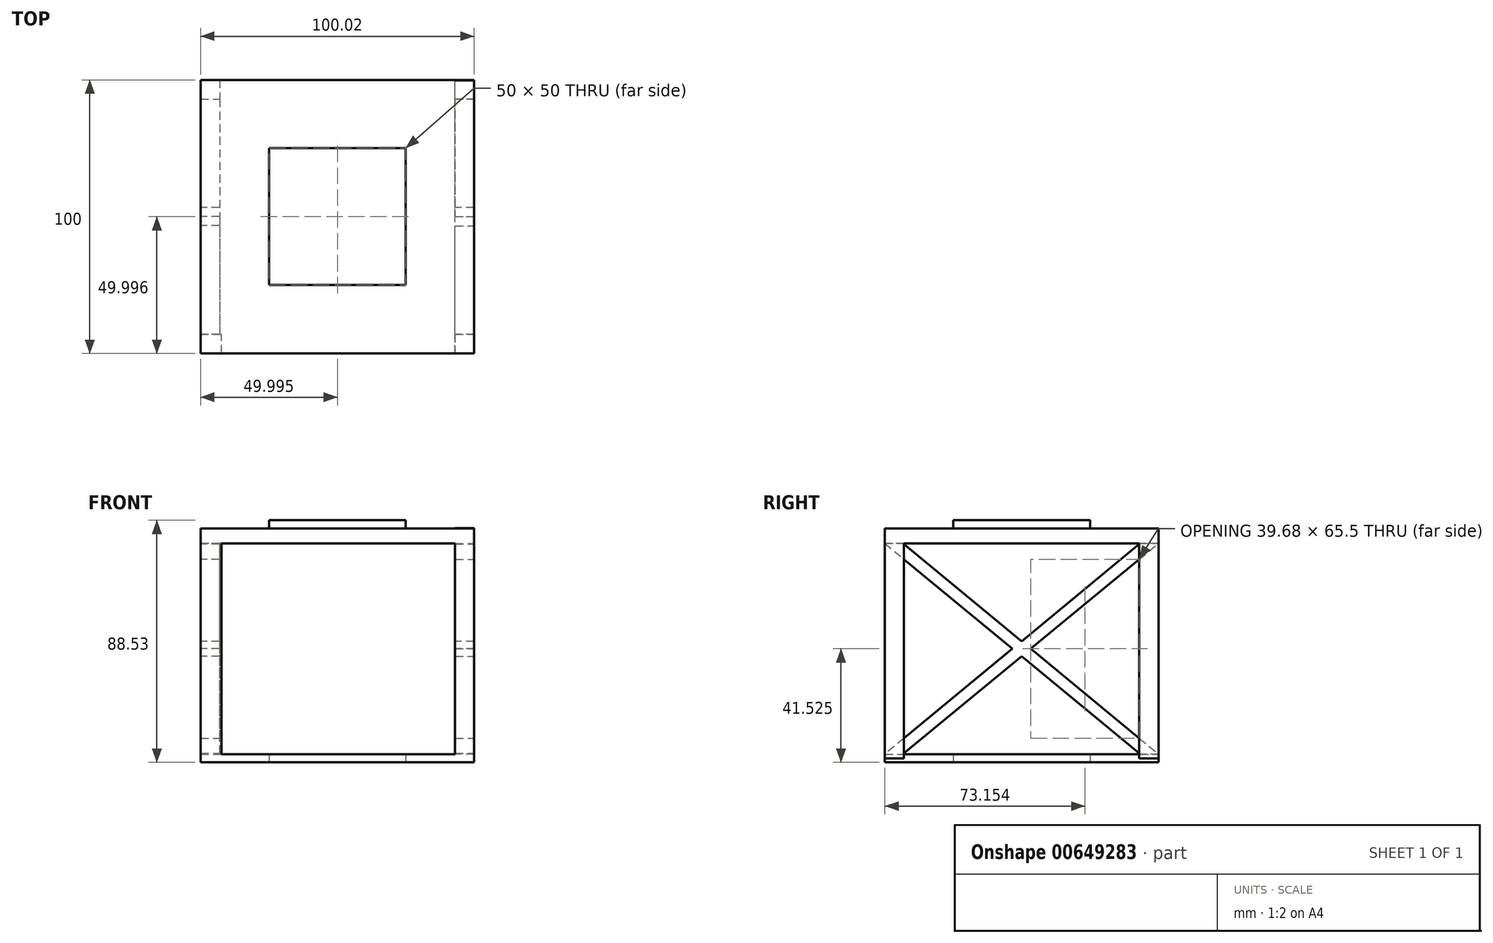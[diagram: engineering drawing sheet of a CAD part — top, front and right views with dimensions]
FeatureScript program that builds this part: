
annotation { "Feature Type Name" : "Feature", "Feature Type Description" : "" }
export const myFeature = defineFeature(function(context is Context, id is Id, definition is map)
    precondition{}
    {
        {
            var Q0;
            Q0=qCreatedBy(makeId("Top.planeOp"),FACE);
            var sketch = newSketch(context, id + "F0", { "sketchPlane" : qUnion([Q0])});
            skLineSegment(sketch, "E0.bottom", {"start": v(-44.37, 46.98) * mm, "end": v(55.63, 46.98) * mm});
            skLineSegment(sketch, "E0.top", {"start": v(-44.37, -53.02) * mm, "end": v(55.63, -53.02) * mm});
            skLineSegment(sketch, "E0.left", {"start": v(-44.37, 46.98) * mm, "end": v(-44.37, -53.02) * mm});
            skLineSegment(sketch, "E0.right", {"start": v(55.63, 46.98) * mm, "end": v(55.63, -53.02) * mm});
            skSolve(sketch);
        }
        {
            var Q0;
            Q0 = qSketchRegion(id + "F0", true);
            extrude(context, id + "F1", {"entities" : qUnion([Q0]), "depth" : 3 * mm, "offsetDistance" : 25 * mm});
        }
        {
            var Q0;
            Q0=makeQuery(id+"F1.opExtrude","SWEPT_FACE",FACE,{"disambiguationData":[OSD([sQuery(id+"F0.wireOp",EDGE,"E0.left")])]});
            var sketch = newSketch(context, id + "F2", { "sketchPlane" : qUnion([Q0])});
            skLineSegment(sketch, "E1", {"start": v(-43.98, 0) * mm, "end": v(53.02, 80.05) * mm});
            skLineSegment(sketch, "E2", {"start": v(-46.98, 3) * mm, "end": v(53.02, 85.53) * mm});
            skLineSegment(sketch, "E3", {"start": v(-46.98, 3) * mm, "end": v(-46.98, 0) * mm});
            skLineSegment(sketch, "E4", {"start": v(-46.98, 0) * mm, "end": v(-43.98, 0) * mm});
            skLineSegment(sketch, "E5", {"start": v(53.02, 85.53) * mm, "end": v(53.02, 80.05) * mm});
            skSolve(sketch);
        }
        {
            var Q0;
            Q0 = qSketchRegion(id + "F2", true);
            extrude(context, id + "F3", {"entities" : qUnion([Q0]), "operationType" : NewBodyOperationType.ADD, "oppositeDirection" : true, "depth" : 7 * mm, "offsetDistance" : 25 * mm});
        }
        {
            var Q0;
            Q0=makeQuery(id+"F3.boolean.opBoolean","MERGE",FACE,{"derivedFrom":[makeQuery(id+"F1.opExtrude","SWEPT_FACE",FACE,{"disambiguationData":[OSD([sQuery(id+"F0.wireOp",EDGE,"E0.left")])]}),makeQuery(id+"F3.opExtrude","CAP_FACE",FACE,{"disambiguationData":[OSD([sQuery(id+"F2.wireOp",EDGE,"E1"),sQuery(id+"F2.wireOp",EDGE,"E2"),sQuery(id+"F2.wireOp",EDGE,"E3"),sQuery(id+"F2.wireOp",EDGE,"E4"),sQuery(id+"F2.wireOp",EDGE,"E5")])],"isStart":true})]});
            var sketch = newSketch(context, id + "F4", { "sketchPlane" : qUnion([Q0])});
            skLineSegment(sketch, "E6", {"start": v(50.02, 0) * mm, "end": v(-46.98, 80.05) * mm});
            skLineSegment(sketch, "E7", {"start": v(53.02, 3) * mm, "end": v(-46.98, 85.53) * mm});
            skLineSegment(sketch, "E8", {"start": v(-46.98, 85.53) * mm, "end": v(-46.98, 80.05) * mm});
            skLineSegment(sketch, "E9", {"start": v(50.02, 0) * mm, "end": v(53.02, 0) * mm});
            skLineSegment(sketch, "E10", {"start": v(53.02, 0) * mm, "end": v(53.02, 3) * mm});
            skSolve(sketch);
        }
        {
            var Q0;
            Q0 = qSketchRegion(id + "F4", true);
            extrude(context, id + "F5", {"entities" : qUnion([Q0]), "operationType" : NewBodyOperationType.ADD, "oppositeDirection" : true, "depth" : 7 * mm, "offsetDistance" : 25 * mm});
        }
        {
            var Q0;
            Q0=makeQuery(id+"F1.opExtrude","SWEPT_FACE",FACE,{"disambiguationData":[OSD([sQuery(id+"F0.wireOp",EDGE,"E0.right")])]});
            var sketch = newSketch(context, id + "F6", { "sketchPlane" : qUnion([Q0])});
            skLineSegment(sketch, "E11", {"start": v(-50.02, 0) * mm, "end": v(46.98, 80.05) * mm});
            skLineSegment(sketch, "E12", {"start": v(-50.02, 0) * mm, "end": v(-53.02, 0) * mm});
            skLineSegment(sketch, "E13", {"start": v(-53.02, 0) * mm, "end": v(-53.02, 3) * mm});
            skLineSegment(sketch, "E14", {"start": v(-53.02, 3) * mm, "end": v(46.98, 85.64) * mm});
            skLineSegment(sketch, "E15", {"start": v(46.98, 85.64) * mm, "end": v(46.98, 80.05) * mm});
            skSolve(sketch);
        }
        {
            var Q0;
            Q0 = qSketchRegion(id + "F6", true);
            extrude(context, id + "F7", {"entities" : qUnion([Q0]), "operationType" : NewBodyOperationType.ADD, "oppositeDirection" : true, "depth" : 7 * mm, "offsetDistance" : 25 * mm});
        }
        {
            var Q0;
            Q0=makeQuery(id+"F7.boolean.opBoolean","MERGE",FACE,{"derivedFrom":[makeQuery(id+"F1.opExtrude","SWEPT_FACE",FACE,{"disambiguationData":[OSD([sQuery(id+"F0.wireOp",EDGE,"E0.right")])]}),makeQuery(id+"F7.opExtrude","CAP_FACE",FACE,{"disambiguationData":[OSD([sQuery(id+"F6.wireOp",EDGE,"E11"),sQuery(id+"F6.wireOp",EDGE,"E12"),sQuery(id+"F6.wireOp",EDGE,"E13"),sQuery(id+"F6.wireOp",EDGE,"E14"),sQuery(id+"F6.wireOp",EDGE,"E15")])],"isStart":true})]});
            var sketch = newSketch(context, id + "F8", { "sketchPlane" : qUnion([Q0])});
            skLineSegment(sketch, "E16", {"start": v(43.98, 0) * mm, "end": v(-53.02, 80.05) * mm});
            skLineSegment(sketch, "E17", {"start": v(-53.02, 80.05) * mm, "end": v(-53.02, 85.55) * mm});
            skLineSegment(sketch, "E18", {"start": v(-53.02, 85.55) * mm, "end": v(46.98, 3) * mm});
            skLineSegment(sketch, "E19", {"start": v(46.98, 3) * mm, "end": v(46.98, 0) * mm});
            skLineSegment(sketch, "E20", {"start": v(46.98, 0) * mm, "end": v(43.98, 0) * mm});
            skSolve(sketch);
        }
        {
            var Q0;
            Q0 = qSketchRegion(id + "F8", true);
            extrude(context, id + "F9", {"entities" : qUnion([Q0]), "operationType" : NewBodyOperationType.ADD, "oppositeDirection" : true, "depth" : 7 * mm, "offsetDistance" : 25 * mm});
        }
        {
            var Q0;
            Q0=makeQuery(id+"F3.opExtrude","SWEPT_FACE",FACE,{"disambiguationData":[OSD([sQuery(id+"F2.wireOp",EDGE,"E5")])]});
            var sketch = newSketch(context, id + "F10", { "sketchPlane" : qUnion([Q0])});
            skLineSegment(sketch, "E21.bottom", {"start": v(-44.37, 85.53) * mm, "end": v(55.65, 85.53) * mm});
            skLineSegment(sketch, "E21.top", {"start": v(-44.37, 80.05) * mm, "end": v(55.65, 80.05) * mm});
            skLineSegment(sketch, "E21.left", {"start": v(-44.37, 85.53) * mm, "end": v(-44.37, 80.05) * mm});
            skLineSegment(sketch, "E21.right", {"start": v(55.65, 85.53) * mm, "end": v(55.65, 80.05) * mm});
            skSolve(sketch);
        }
        {
            var Q0;
            Q0 = qSketchRegion(id + "F10", true);
            extrude(context, id + "F11", {"entities" : qUnion([Q0]), "operationType" : NewBodyOperationType.ADD, "oppositeDirection" : true, "depth" : 100 * mm, "offsetDistance" : 25 * mm});
        }
        {
            var Q0;
            Q0=makeQuery(id+"F11.opExtrude","SWEPT_FACE",FACE,{"disambiguationData":[OSD([sQuery(id+"F10.wireOp",EDGE,"E21.bottom")])]});
            var sketch = newSketch(context, id + "F12", { "sketchPlane" : qUnion([Q0])});
            skLineSegment(sketch, "E22.bottom", {"start": v(-19.37, 21.98) * mm, "end": v(30.63, 21.98) * mm});
            skLineSegment(sketch, "E22.top", {"start": v(-19.37, -28.02) * mm, "end": v(30.63, -28.02) * mm});
            skLineSegment(sketch, "E22.left", {"start": v(-19.37, 21.98) * mm, "end": v(-19.37, -28.02) * mm});
            skLineSegment(sketch, "E22.right", {"start": v(30.63, 21.98) * mm, "end": v(30.63, -28.02) * mm});
            skSolve(sketch);
        }
        {
            var Q0;
            Q0 = qSketchRegion(id + "F12", true);
            extrude(context, id + "F13", {"entities" : qUnion([Q0]), "operationType" : NewBodyOperationType.ADD, "depth" : 3 * mm, "offsetDistance" : 25 * mm});
        }
        {
            var Q0;
            Q0=makeQuery(id+"F1.opExtrude","CAP_FACE",FACE,{"disambiguationData":[OSD([sQuery(id+"F0.wireOp",EDGE,"E0.bottom"),sQuery(id+"F0.wireOp",EDGE,"E0.top"),sQuery(id+"F0.wireOp",EDGE,"E0.left"),sQuery(id+"F0.wireOp",EDGE,"E0.right")])],"isStart":true});
            var sketch = newSketch(context, id + "F14", { "sketchPlane" : qUnion([Q0])});
            skLineSegment(sketch, "E23.bottom", {"start": v(-19.37, 28.02) * mm, "end": v(30.63, 28.02) * mm});
            skLineSegment(sketch, "E23.top", {"start": v(-19.37, -21.98) * mm, "end": v(30.63, -21.98) * mm});
            skLineSegment(sketch, "E23.left", {"start": v(-19.37, 28.02) * mm, "end": v(-19.37, -21.98) * mm});
            skLineSegment(sketch, "E23.right", {"start": v(30.63, 28.02) * mm, "end": v(30.63, -21.98) * mm});
            skSolve(sketch);
        }
        {
            var Q0;
            Q0 = qSketchRegion(id + "F14", true);
            extrude(context, id + "F15", {"entities" : qUnion([Q0]), "operationType" : NewBodyOperationType.REMOVE, "oppositeDirection" : true, "depth" : 25 * mm, "offsetDistance" : 25 * mm});
        }
        {
            var Q0;
            Q0=makeQuery(id+"F11.opExtrude","SWEPT_FACE",FACE,{"disambiguationData":[OSD([sQuery(id+"F10.wireOp",EDGE,"E21.bottom")])]});
            var sketch = newSketch(context, id + "F16", { "sketchPlane" : qUnion([Q0])});
            skLineSegment(sketch, "E24.bottom", {"start": v(-44.37, -53.02) * mm, "end": v(-36.7, -53.02) * mm});
            skLineSegment(sketch, "E24.top", {"start": v(-44.37, -46.02) * mm, "end": v(-36.7, -46.02) * mm});
            skLineSegment(sketch, "E24.left", {"start": v(-44.37, -53.02) * mm, "end": v(-44.37, -46.02) * mm});
            skLineSegment(sketch, "E24.right", {"start": v(-36.7, -53.02) * mm, "end": v(-36.7, -46.02) * mm});
            skSolve(sketch);
        }
        {
            var Q0;
            Q0 = qSketchRegion(id + "F16", true);
            extrude(context, id + "F17", {"entities" : qUnion([Q0]), "operationType" : NewBodyOperationType.ADD, "oppositeDirection" : true, "depth" : 84.7 * mm, "offsetDistance" : 25 * mm});
        }
        {
            var Q0;
            Q0=makeQuery(id+"F11.opExtrude","SWEPT_FACE",FACE,{"disambiguationData":[OSD([sQuery(id+"F10.wireOp",EDGE,"E21.bottom")])]});
            var sketch = newSketch(context, id + "F18", { "sketchPlane" : qUnion([Q0])});
            skLineSegment(sketch, "E25.bottom", {"start": v(-44.37, 46.98) * mm, "end": v(-37.37, 46.98) * mm});
            skLineSegment(sketch, "E25.top", {"start": v(-44.37, 39.98) * mm, "end": v(-37.37, 39.98) * mm});
            skLineSegment(sketch, "E25.left", {"start": v(-44.37, 46.98) * mm, "end": v(-44.37, 39.98) * mm});
            skLineSegment(sketch, "E25.right", {"start": v(-37.37, 46.98) * mm, "end": v(-37.37, 39.98) * mm});
            skLineSegment(sketch, "E26.bottom", {"start": v(55.65, 46.98) * mm, "end": v(48.65, 46.98) * mm});
            skLineSegment(sketch, "E26.top", {"start": v(55.65, 39.98) * mm, "end": v(48.65, 39.98) * mm});
            skLineSegment(sketch, "E26.left", {"start": v(55.65, 46.98) * mm, "end": v(55.65, 39.98) * mm});
            skLineSegment(sketch, "E26.right", {"start": v(48.65, 46.98) * mm, "end": v(48.65, 39.98) * mm});
            skLineSegment(sketch, "E27.bottom", {"start": v(55.65, -53.02) * mm, "end": v(48.65, -53.02) * mm});
            skLineSegment(sketch, "E27.top", {"start": v(55.65, -46.02) * mm, "end": v(48.65, -46.02) * mm});
            skLineSegment(sketch, "E27.left", {"start": v(55.65, -53.02) * mm, "end": v(55.65, -46.02) * mm});
            skLineSegment(sketch, "E27.right", {"start": v(48.65, -53.02) * mm, "end": v(48.65, -46.02) * mm});
            skSolve(sketch);
        }
        {
            var Q0;
            Q0 = qSketchRegion(id + "F18", true);
            extrude(context, id + "F19", {"entities" : qUnion([Q0]), "operationType" : NewBodyOperationType.ADD, "oppositeDirection" : true, "depth" : 84.1 * mm, "offsetDistance" : 25 * mm});
        }
    });
